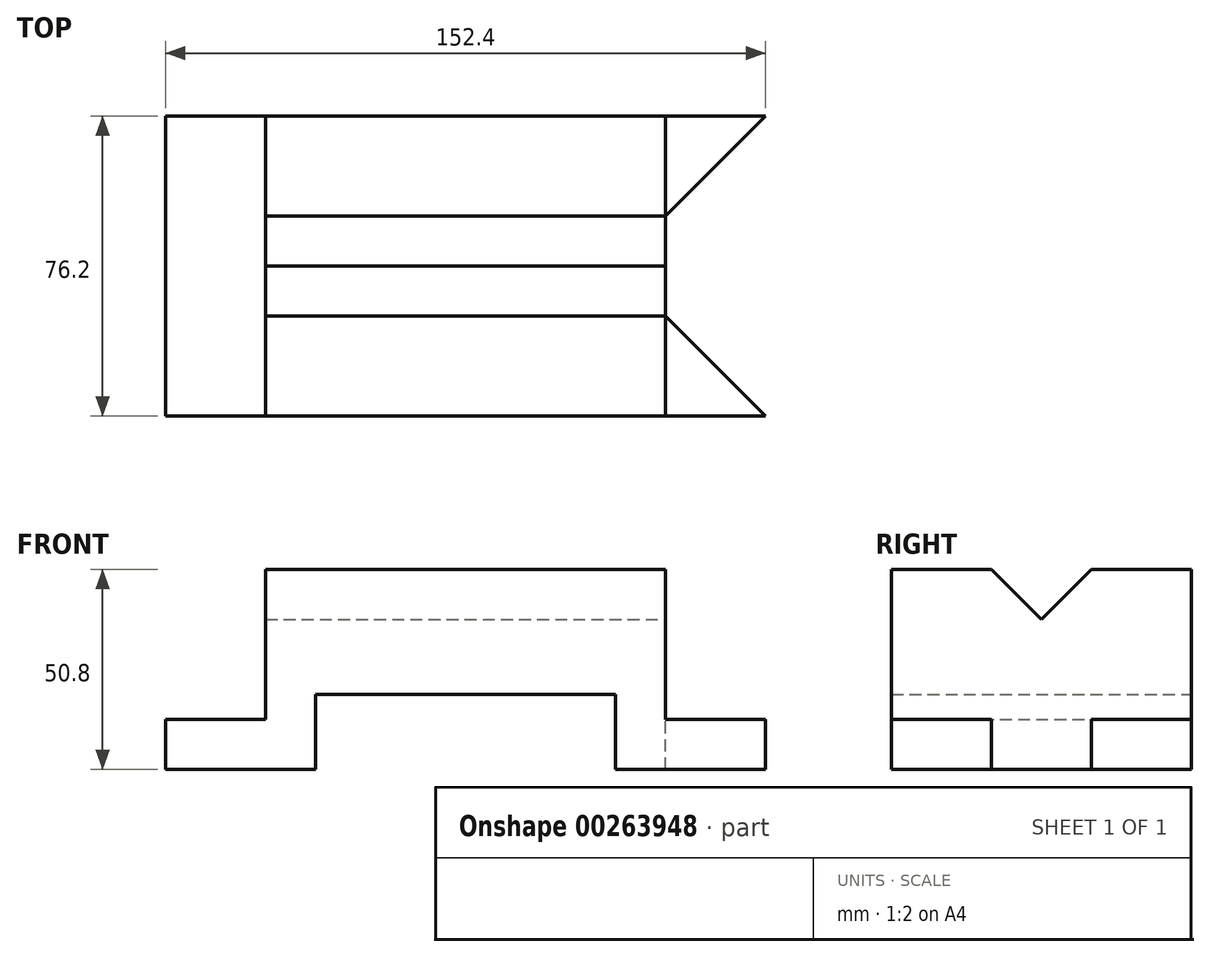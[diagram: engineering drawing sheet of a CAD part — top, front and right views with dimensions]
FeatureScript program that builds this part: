
annotation { "Feature Type Name" : "Feature", "Feature Type Description" : "" }
export const myFeature = defineFeature(function(context is Context, id is Id, definition is map)
    precondition{}
    {
        {
            var Q0;
            Q0=qCreatedBy(makeId("Front.planeOp"),FACE);
            var sketch = newSketch(context, id + "F0", { "sketchPlane" : qUnion([Q0])});
            skLineSegment(sketch, "E0", {"start": v(-75.4, 0) * mm, "end": v(-37.3, 0) * mm});
            skLineSegment(sketch, "E1", {"start": v(-75.4, 0) * mm, "end": v(-75.4, 12.7) * mm});
            skLineSegment(sketch, "E2", {"start": v(-75.4, 12.7) * mm, "end": v(-50, 12.7) * mm});
            skLineSegment(sketch, "E3", {"start": v(-50, 12.7) * mm, "end": v(-50, 50.8) * mm});
            skLineSegment(sketch, "E4", {"start": v(-50, 50.8) * mm, "end": v(51.6, 50.8) * mm});
            skLineSegment(sketch, "E5", {"start": v(51.6, 50.8) * mm, "end": v(51.6, 12.7) * mm});
            skLineSegment(sketch, "E6", {"start": v(51.6, 12.7) * mm, "end": v(77, 12.7) * mm});
            skLineSegment(sketch, "E7", {"start": v(77, 12.7) * mm, "end": v(77, 0) * mm});
            skLineSegment(sketch, "E8", {"start": v(77, 0) * mm, "end": v(38.9, 0) * mm});
            skLineSegment(sketch, "E9", {"start": v(38.9, 0) * mm, "end": v(38.9, 19.05) * mm});
            skLineSegment(sketch, "E10", {"start": v(38.9, 19.05) * mm, "end": v(-37.3, 19.05) * mm});
            skLineSegment(sketch, "E11", {"start": v(-37.3, 19.05) * mm, "end": v(-37.3, 0) * mm});
            skSolve(sketch);
        }
        {
            var Q0;
            Q0 = qSketchRegion(id + "F0", true);
            extrude(context, id + "F1", {"entities" : qUnion([Q0]), "depth" : 76.2 * mm});
        }
        {
            var Q0;
            Q0=makeQuery(id+"F1.opExtrude","SWEPT_FACE",FACE,{"disambiguationData":[OSD([sQuery(id+"F0.wireOp",EDGE,"E6")])]});
            var sketch = newSketch(context, id + "F2", { "sketchPlane" : qUnion([Q0])});
            skLineSegment(sketch, "E12", {"start": v(51.6, -76.2) * mm, "end": v(51.6, -50.8) * mm});
            skLineSegment(sketch, "E13", {"start": v(51.6, -50.8) * mm, "end": v(77, -76.2) * mm});
            skLineSegment(sketch, "E14", {"start": v(77, -76.2) * mm, "end": v(51.6, -76.2) * mm});
            skLineSegment(sketch, "E15", {"start": v(51.6, 0) * mm, "end": v(51.6, -25.4) * mm});
            skLineSegment(sketch, "E16", {"start": v(51.6, -25.4) * mm, "end": v(77, 0) * mm});
            skLineSegment(sketch, "E17", {"start": v(77, 0) * mm, "end": v(51.6, 0) * mm});
            skSolve(sketch);
        }
        {
            var Q0;
            {var subQ0=sQuery(id+"F2.wireOp",EDGE,"E13");Q0=makeQuery(id+"F2.imprint","IMPRINT",FACE,{"disambiguationData":[TD([[makeQuery(id+"F2.imprint","IMPRINT",EDGE,{"derivedFrom":subQ0}),1.0]])]});}
            extrude(context, id + "F3", {"entities" : qUnion([Q0]), "operationType" : NewBodyOperationType.REMOVE, "oppositeDirection" : true, "depth" : 25.4 * mm});
        }
        {
            var Q0;
            {var subQ0=sQuery(id+"F0.wireOp",EDGE,"E5");Q0=makeQuery(id+"F3.boolean.opBoolean","MERGE",FACE,{"derivedFrom":[makeQuery(id+"F1.opExtrude","SWEPT_FACE",FACE,{"disambiguationData":[OSD([subQ0])]}),makeQuery(id+"F3.opExtrude","SWEPT_FACE",FACE,{"disambiguationData":[OSD([subQ0,sQuery(id+"F0.wireOp",EDGE,"E6")])]})]});}
            var sketch = newSketch(context, id + "F4", { "sketchPlane" : qUnion([Q0])});
            skLineSegment(sketch, "E18", {"start": v(-76.2, 50.8) * mm, "end": v(-50.8, 50.8) * mm});
            skLineSegment(sketch, "E19", {"start": v(0, 50.8) * mm, "end": v(-25.4, 50.8) * mm});
            skLineSegment(sketch, "E20", {"start": v(-25.4, 50.8) * mm, "end": v(-25.4, 38.1) * mm, "construction": true});
            skLineSegment(sketch, "E21", {"start": v(-50.8, 50.8) * mm, "end": v(-50.8, 38.1) * mm, "construction": true});
            skLineSegment(sketch, "E22", {"start": v(-50.8, 38.1) * mm, "end": v(-25.4, 38.1) * mm, "construction": true});
            skLineSegment(sketch, "E23", {"start": v(-50.8, 50.8) * mm, "end": v(-38.1, 38.1) * mm});
            skLineSegment(sketch, "E24", {"start": v(-38.1, 38.1) * mm, "end": v(-25.4, 50.8) * mm});
            skSolve(sketch);
        }
        {
            var Q0;
            {var subQ0=sQuery(id+"F4.wireOp",EDGE,"E23");Q0=makeQuery(id+"F4.imprint","IMPRINT",FACE,{"disambiguationData":[TD([[makeQuery(id+"F4.imprint","IMPRINT",EDGE,{"derivedFrom":subQ0}),1.0]])]});}
            extrude(context, id + "F5", {"entities" : qUnion([Q0]), "operationType" : NewBodyOperationType.REMOVE, "endBound" : BoundingType.UP_TO_NEXT, "oppositeDirection" : true, "depth" : 25.4 * mm});
        }
    });
